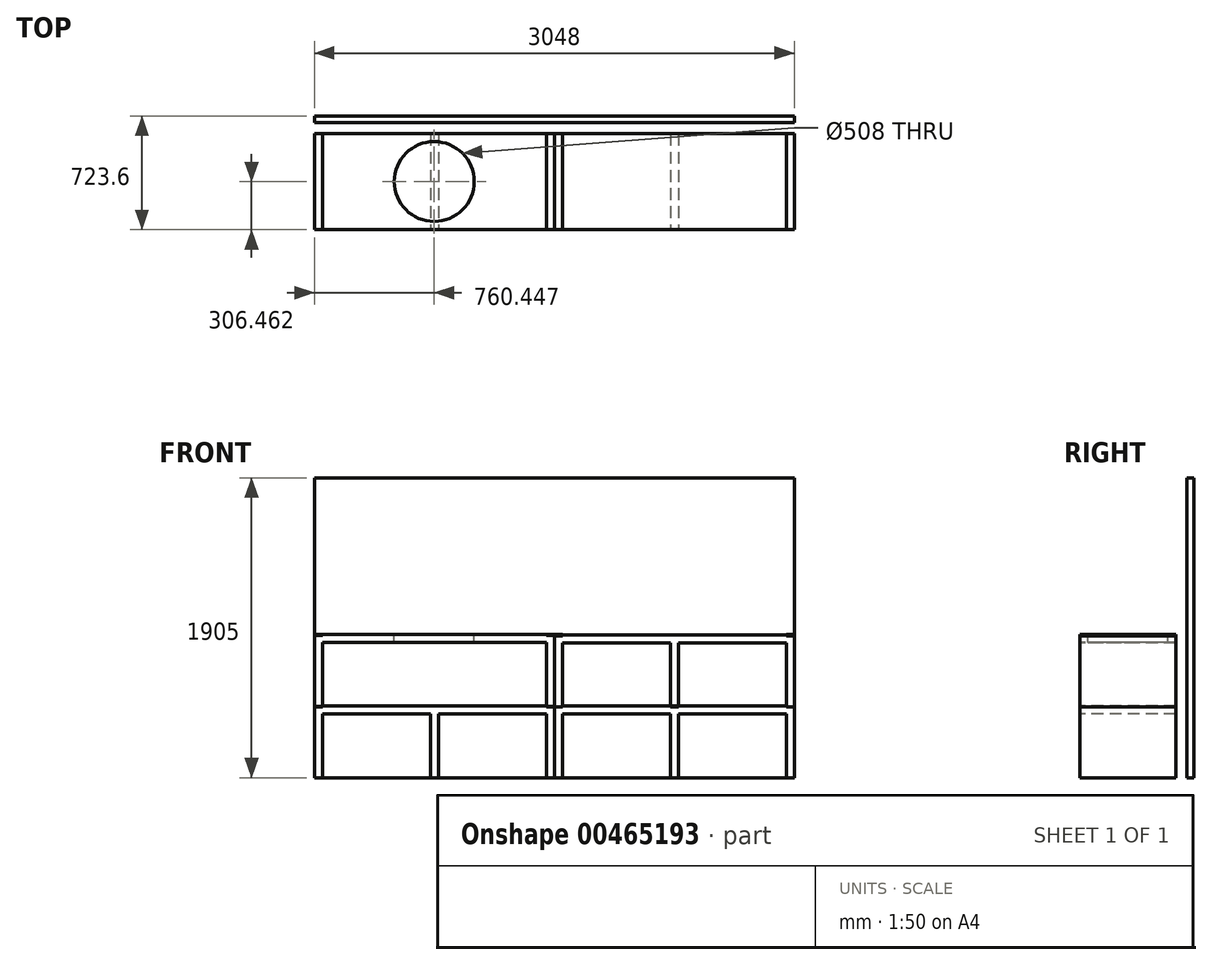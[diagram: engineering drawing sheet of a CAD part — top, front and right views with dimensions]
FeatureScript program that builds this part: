
annotation { "Feature Type Name" : "Feature", "Feature Type Description" : "" }
export const myFeature = defineFeature(function(context is Context, id is Id, definition is map)
    precondition{}
    {
        {
            var Q0;
            Q0=qCreatedBy(makeId("Front.planeOp"),FACE);
            var sketch = newSketch(context, id + "F0", { "sketchPlane" : qUnion([Q0])});
            skLineSegment(sketch, "E0", {"start": v(-50.8, -209.2) * mm, "end": v(-50.8, 241.64) * mm});
            skLineSegment(sketch, "E1", {"start": v(-50.8, 241.64) * mm, "end": v(0, 241.64) * mm});
            skLineSegment(sketch, "E2", {"start": v(0, 241.64) * mm, "end": v(0, 248) * mm});
            skLineSegment(sketch, "E3", {"start": v(0, 248) * mm, "end": v(1422.4, 248) * mm});
            skLineSegment(sketch, "E4", {"start": v(1422.4, 248) * mm, "end": v(1422.4, 241.64) * mm});
            skLineSegment(sketch, "E5", {"start": v(1422.4, 241.64) * mm, "end": v(1473.2, 241.64) * mm});
            skLineSegment(sketch, "E6", {"start": v(1473.2, 241.64) * mm, "end": v(1473.2, -209.2) * mm});
            skLineSegment(sketch, "E7", {"start": v(1473.2, -209.2) * mm, "end": v(1422.4, -209.2) * mm});
            skLineSegment(sketch, "E8", {"start": v(1422.4, -209.2) * mm, "end": v(1422.4, 197.2) * mm});
            skLineSegment(sketch, "E9", {"start": v(1422.4, 197.2) * mm, "end": v(736.6, 197.2) * mm});
            skLineSegment(sketch, "E10", {"start": v(736.6, 197.2) * mm, "end": v(736.6, -209.2) * mm});
            skLineSegment(sketch, "E11", {"start": v(736.6, -209.2) * mm, "end": v(685.8, -209.2) * mm});
            skLineSegment(sketch, "E12", {"start": v(685.8, -209.2) * mm, "end": v(685.8, 197.2) * mm});
            skLineSegment(sketch, "E13", {"start": v(685.8, 197.2) * mm, "end": v(0, 197.2) * mm});
            skLineSegment(sketch, "E14", {"start": v(0, 197.2) * mm, "end": v(0, -209.2) * mm});
            skLineSegment(sketch, "E15", {"start": v(0, -209.2) * mm, "end": v(-50.8, -209.2) * mm});
            skSolve(sketch);
        }
        {
            var Q0;
            Q0 = qSketchRegion(id + "F0", true);
            extrude(context, id + "F1", {"entities" : qUnion([Q0]), "depth" : -609.6 * mm});
        }
        {
            var Q0;
            Q0=makeQuery(id+"F1.opExtrude","CAP_FACE",FACE,{"disambiguationData":[OSD([sQuery(id+"F0.wireOp",EDGE,"E0"),sQuery(id+"F0.wireOp",EDGE,"E1"),sQuery(id+"F0.wireOp",EDGE,"E2"),sQuery(id+"F0.wireOp",EDGE,"E3"),sQuery(id+"F0.wireOp",EDGE,"E4"),sQuery(id+"F0.wireOp",EDGE,"E5"),sQuery(id+"F0.wireOp",EDGE,"E6"),sQuery(id+"F0.wireOp",EDGE,"E7"),sQuery(id+"F0.wireOp",EDGE,"E8"),sQuery(id+"F0.wireOp",EDGE,"E9"),sQuery(id+"F0.wireOp",EDGE,"E10"),sQuery(id+"F0.wireOp",EDGE,"E11"),sQuery(id+"F0.wireOp",EDGE,"E12"),sQuery(id+"F0.wireOp",EDGE,"E13"),sQuery(id+"F0.wireOp",EDGE,"E14"),sQuery(id+"F0.wireOp",EDGE,"E15")])],"isStart":true});
            var sketch = newSketch(context, id + "F2", { "sketchPlane" : qUnion([Q0])});
            skLineSegment(sketch, "E16", {"start": v(-50.8, 273.91) * mm, "end": v(-50.8, 724.76) * mm});
            skLineSegment(sketch, "E17", {"start": v(0, 724.76) * mm, "end": v(-50.8, 724.76) * mm});
            skLineSegment(sketch, "E18", {"start": v(0, 724.76) * mm, "end": v(0, 731.11) * mm});
            skLineSegment(sketch, "E19", {"start": v(0, 731.11) * mm, "end": v(1422.4, 731.11) * mm});
            skLineSegment(sketch, "E20", {"start": v(1422.4, 731.11) * mm, "end": v(1422.4, 724.76) * mm});
            skLineSegment(sketch, "E21", {"start": v(1422.4, 724.76) * mm, "end": v(1473.2, 724.76) * mm});
            skLineSegment(sketch, "E22", {"start": v(1473.2, 724.76) * mm, "end": v(1473.2, 273.91) * mm});
            skLineSegment(sketch, "E23", {"start": v(1473.2, 273.91) * mm, "end": v(1422.4, 273.91) * mm});
            skLineSegment(sketch, "E24", {"start": v(1422.4, 273.91) * mm, "end": v(1422.4, 680.31) * mm});
            skLineSegment(sketch, "E25", {"start": v(1422.4, 680.31) * mm, "end": v(0, 680.31) * mm});
            skLineSegment(sketch, "E26", {"start": v(0, 680.31) * mm, "end": v(0, 273.91) * mm});
            skLineSegment(sketch, "E27", {"start": v(0, 273.91) * mm, "end": v(-50.8, 273.91) * mm});
            skSolve(sketch);
        }
        {
            var Q0;
            Q0 = qSketchRegion(id + "F2", true);
            extrude(context, id + "F3", {"entities" : qUnion([Q0]), "depth" : -609.6 * mm});
        }
        {
            var Q0;
            Q0=makeQuery(id+"F3.opExtrude","SWEPT_BODY",BODY,{"disambiguationData":[OSD([sQuery(id+"F2.wireOp",EDGE,"E16"),sQuery(id+"F2.wireOp",EDGE,"E17"),sQuery(id+"F2.wireOp",EDGE,"E18"),sQuery(id+"F2.wireOp",EDGE,"E19"),sQuery(id+"F2.wireOp",EDGE,"E20"),sQuery(id+"F2.wireOp",EDGE,"E21"),sQuery(id+"F2.wireOp",EDGE,"E22"),sQuery(id+"F2.wireOp",EDGE,"E23"),sQuery(id+"F2.wireOp",EDGE,"E24"),sQuery(id+"F2.wireOp",EDGE,"E25"),sQuery(id+"F2.wireOp",EDGE,"E26"),sQuery(id+"F2.wireOp",EDGE,"E27")])]});
            transform(context, id + "F4", {"entities" : qUnion([Q0]), "transformType" : TransformType.TRANSLATION_3D, "dx" : 0 * mm, "dy" : 0 * mm, "dz" : -31.75 * mm, "makeCopy" : true});
        }
        {
            var Q0;
            Q0=makeQuery(id+"F3.opExtrude","SWEPT_BODY",BODY,{"disambiguationData":[OSD([sQuery(id+"F2.wireOp",EDGE,"E16"),sQuery(id+"F2.wireOp",EDGE,"E17"),sQuery(id+"F2.wireOp",EDGE,"E18"),sQuery(id+"F2.wireOp",EDGE,"E19"),sQuery(id+"F2.wireOp",EDGE,"E20"),sQuery(id+"F2.wireOp",EDGE,"E21"),sQuery(id+"F2.wireOp",EDGE,"E22"),sQuery(id+"F2.wireOp",EDGE,"E23"),sQuery(id+"F2.wireOp",EDGE,"E24"),sQuery(id+"F2.wireOp",EDGE,"E25"),sQuery(id+"F2.wireOp",EDGE,"E26"),sQuery(id+"F2.wireOp",EDGE,"E27")])]});
            deleteBodies(context, id + "F5", {"entities" : qUnion([Q0])});
        }
        {
            var Q0;
            Q0=makeQuery(id+"F4.opPattern","COPY",FACE,{"derivedFrom":makeQuery(id+"F3.opExtrude","SWEPT_FACE",FACE,{"disambiguationData":[OSD([sQuery(id+"F2.wireOp",EDGE,"E19")])]}),"instanceName":"1"});
            var sketch = newSketch(context, id + "F6", { "sketchPlane" : qUnion([Q0])});
            skPoint(sketch, "E28", {"position": v(709.65, 306.46) * mm});
            skSolve(sketch);
        }
        {
            var Q0;
            Q0=sQuery(id+"F6.wireOp",VERTEX,"E28");
            var Q1;
            Q1=makeQuery(id+"F4.opPattern","COPY",BODY,{"derivedFrom":makeQuery(id+"F3.opExtrude","SWEPT_BODY",BODY,{"disambiguationData":[OSD([sQuery(id+"F2.wireOp",EDGE,"E16"),sQuery(id+"F2.wireOp",EDGE,"E17"),sQuery(id+"F2.wireOp",EDGE,"E18"),sQuery(id+"F2.wireOp",EDGE,"E19"),sQuery(id+"F2.wireOp",EDGE,"E20"),sQuery(id+"F2.wireOp",EDGE,"E21"),sQuery(id+"F2.wireOp",EDGE,"E22"),sQuery(id+"F2.wireOp",EDGE,"E23"),sQuery(id+"F2.wireOp",EDGE,"E24"),sQuery(id+"F2.wireOp",EDGE,"E25"),sQuery(id+"F2.wireOp",EDGE,"E26"),sQuery(id+"F2.wireOp",EDGE,"E27")])]}),"instanceName":"1"});
            hole(context, id + "F7", {"style" : HoleStyle.SIMPLE, "endStyle" : HoleEndStyle.BLIND, "holeDiameter" : 508 * mm, "holeDepth" : 50.8 * mm, "isTappedThrough" : true, "tappedDepth" : 12.7 * mm, "tapClearance" : 3, "locations" : qUnion([Q0]), "scope" : qUnion([Q1])});
        }
        {
            var Q0;
            Q0=makeQuery(id+"F4.opPattern","COPY",FACE,{"derivedFrom":makeQuery(id+"F3.opExtrude","CAP_FACE",FACE,{"disambiguationData":[OSD([sQuery(id+"F2.wireOp",EDGE,"E16"),sQuery(id+"F2.wireOp",EDGE,"E17"),sQuery(id+"F2.wireOp",EDGE,"E18"),sQuery(id+"F2.wireOp",EDGE,"E19"),sQuery(id+"F2.wireOp",EDGE,"E20"),sQuery(id+"F2.wireOp",EDGE,"E21"),sQuery(id+"F2.wireOp",EDGE,"E22"),sQuery(id+"F2.wireOp",EDGE,"E23"),sQuery(id+"F2.wireOp",EDGE,"E24"),sQuery(id+"F2.wireOp",EDGE,"E25"),sQuery(id+"F2.wireOp",EDGE,"E26"),sQuery(id+"F2.wireOp",EDGE,"E27")])],"isStart":true}),"instanceName":"1"});
            var sketch = newSketch(context, id + "F8", { "sketchPlane" : qUnion([Q0])});
            skLineSegment(sketch, "E29.bottom", {"start": v(-50.8, 727.26) * mm, "end": v(0, 727.26) * mm});
            skLineSegment(sketch, "E29.top", {"start": v(-50.8, 720.91) * mm, "end": v(0, 720.91) * mm});
            skLineSegment(sketch, "E29.left", {"start": v(-50.8, 727.26) * mm, "end": v(-50.8, 720.91) * mm});
            skLineSegment(sketch, "E29.right", {"start": v(0, 727.26) * mm, "end": v(0, 720.91) * mm});
            skSolve(sketch);
        }
        {
            var Q0;
            Q0 = qSketchRegion(id + "F8", true);
            extrude(context, id + "F9", {"entities" : qUnion([Q0]), "depth" : -609.6 * mm});
        }
        {
            var Q0;
            Q0=makeQuery(id+"F9.opExtrude","SWEPT_BODY",BODY,{"disambiguationData":[OSD([sQuery(id+"F8.wireOp",EDGE,"E29.bottom"),sQuery(id+"F8.wireOp",EDGE,"E29.top"),sQuery(id+"F8.wireOp",EDGE,"E29.left"),sQuery(id+"F8.wireOp",EDGE,"E29.right")])]});
            transform(context, id + "F10", {"entities" : qUnion([Q0]), "transformType" : TransformType.TRANSLATION_3D, "dx" : 0 * mm, "dy" : 0 * mm, "dz" : -27.94 * mm, "makeCopy" : true});
        }
        {
            var Q0;
            Q0=makeQuery(id+"F9.opExtrude","SWEPT_BODY",BODY,{"disambiguationData":[OSD([sQuery(id+"F8.wireOp",EDGE,"E29.bottom"),sQuery(id+"F8.wireOp",EDGE,"E29.top"),sQuery(id+"F8.wireOp",EDGE,"E29.left"),sQuery(id+"F8.wireOp",EDGE,"E29.right")])]});
            deleteBodies(context, id + "F11", {"entities" : qUnion([Q0])});
        }
        {
            var Q0;
            Q0=makeQuery(id+"F10.opPattern","COPY",BODY,{"derivedFrom":makeQuery(id+"F9.opExtrude","SWEPT_BODY",BODY,{"disambiguationData":[OSD([sQuery(id+"F8.wireOp",EDGE,"E29.bottom"),sQuery(id+"F8.wireOp",EDGE,"E29.top"),sQuery(id+"F8.wireOp",EDGE,"E29.left"),sQuery(id+"F8.wireOp",EDGE,"E29.right")])]}),"instanceName":"1"});
            transform(context, id + "F12", {"entities" : qUnion([Q0]), "transformType" : TransformType.TRANSLATION_3D, "dx" : 1473.2 * mm, "dy" : 254 * mm, "dz" : 0 * mm, "makeCopy" : true});
        }
        {
            var Q0;
            Q0=makeQuery(id+"F1.opExtrude","SWEPT_BODY",BODY,{"disambiguationData":[OSD([sQuery(id+"F0.wireOp",EDGE,"E0"),sQuery(id+"F0.wireOp",EDGE,"E1"),sQuery(id+"F0.wireOp",EDGE,"E2"),sQuery(id+"F0.wireOp",EDGE,"E3"),sQuery(id+"F0.wireOp",EDGE,"E4"),sQuery(id+"F0.wireOp",EDGE,"E5"),sQuery(id+"F0.wireOp",EDGE,"E6"),sQuery(id+"F0.wireOp",EDGE,"E7"),sQuery(id+"F0.wireOp",EDGE,"E8"),sQuery(id+"F0.wireOp",EDGE,"E9"),sQuery(id+"F0.wireOp",EDGE,"E10"),sQuery(id+"F0.wireOp",EDGE,"E11"),sQuery(id+"F0.wireOp",EDGE,"E12"),sQuery(id+"F0.wireOp",EDGE,"E13"),sQuery(id+"F0.wireOp",EDGE,"E14"),sQuery(id+"F0.wireOp",EDGE,"E15")])]});
            transform(context, id + "F13", {"entities" : qUnion([Q0]), "transformType" : TransformType.TRANSLATION_3D, "dx" : 1524 * mm, "dy" : 0 * mm, "dz" : 0 * mm, "makeCopy" : true});
        }
        {
            var Q0;
            Q0=makeQuery(id+"F13.opPattern","COPY",BODY,{"derivedFrom":makeQuery(id+"F1.opExtrude","SWEPT_BODY",BODY,{"disambiguationData":[OSD([sQuery(id+"F0.wireOp",EDGE,"E0"),sQuery(id+"F0.wireOp",EDGE,"E1"),sQuery(id+"F0.wireOp",EDGE,"E2"),sQuery(id+"F0.wireOp",EDGE,"E3"),sQuery(id+"F0.wireOp",EDGE,"E4"),sQuery(id+"F0.wireOp",EDGE,"E5"),sQuery(id+"F0.wireOp",EDGE,"E6"),sQuery(id+"F0.wireOp",EDGE,"E7"),sQuery(id+"F0.wireOp",EDGE,"E8"),sQuery(id+"F0.wireOp",EDGE,"E9"),sQuery(id+"F0.wireOp",EDGE,"E10"),sQuery(id+"F0.wireOp",EDGE,"E11"),sQuery(id+"F0.wireOp",EDGE,"E12"),sQuery(id+"F0.wireOp",EDGE,"E13"),sQuery(id+"F0.wireOp",EDGE,"E14"),sQuery(id+"F0.wireOp",EDGE,"E15")])]}),"instanceName":"1"});
            transform(context, id + "F14", {"entities" : qUnion([Q0]), "transformType" : TransformType.TRANSLATION_3D, "dx" : 0 * mm, "dy" : 0 * mm, "dz" : 450.85 * mm, "makeCopy" : true});
        }
        {
            var Q0;
            Q0=makeQuery(id+"F12.opPattern","COPY",BODY,{"derivedFrom":makeQuery(id+"F10.opPattern","COPY",BODY,{"derivedFrom":makeQuery(id+"F9.opExtrude","SWEPT_BODY",BODY,{"disambiguationData":[OSD([sQuery(id+"F8.wireOp",EDGE,"E29.bottom"),sQuery(id+"F8.wireOp",EDGE,"E29.top"),sQuery(id+"F8.wireOp",EDGE,"E29.left"),sQuery(id+"F8.wireOp",EDGE,"E29.right")])]}),"instanceName":"1"}),"instanceName":"1"});
            transform(context, id + "F15", {"entities" : qUnion([Q0]), "transformType" : TransformType.TRANSLATION_3D, "dx" : 50.8 * mm, "dy" : 0 * mm, "dz" : 0 * mm, "makeCopy" : true});
        }
        {
            var Q0;
            Q0=makeQuery(id+"F12.opPattern","COPY",BODY,{"derivedFrom":makeQuery(id+"F10.opPattern","COPY",BODY,{"derivedFrom":makeQuery(id+"F9.opExtrude","SWEPT_BODY",BODY,{"disambiguationData":[OSD([sQuery(id+"F8.wireOp",EDGE,"E29.bottom"),sQuery(id+"F8.wireOp",EDGE,"E29.top"),sQuery(id+"F8.wireOp",EDGE,"E29.left"),sQuery(id+"F8.wireOp",EDGE,"E29.right")])]}),"instanceName":"1"}),"instanceName":"1"});
            transform(context, id + "F16", {"entities" : qUnion([Q0]), "transformType" : TransformType.TRANSLATION_3D, "dx" : 1524 * mm, "dy" : 0 * mm, "dz" : 0 * mm, "makeCopy" : true});
        }
        {
            var Q0;
            Q0=makeQuery(id+"F12.opPattern","COPY",BODY,{"derivedFrom":makeQuery(id+"F10.opPattern","COPY",BODY,{"derivedFrom":makeQuery(id+"F9.opExtrude","SWEPT_BODY",BODY,{"disambiguationData":[OSD([sQuery(id+"F8.wireOp",EDGE,"E29.bottom"),sQuery(id+"F8.wireOp",EDGE,"E29.top"),sQuery(id+"F8.wireOp",EDGE,"E29.left"),sQuery(id+"F8.wireOp",EDGE,"E29.right")])]}),"instanceName":"1"}),"instanceName":"1"});
            var Q1;
            Q1=makeQuery(id+"F15.opPattern","COPY",BODY,{"derivedFrom":makeQuery(id+"F12.opPattern","COPY",BODY,{"derivedFrom":makeQuery(id+"F10.opPattern","COPY",BODY,{"derivedFrom":makeQuery(id+"F9.opExtrude","SWEPT_BODY",BODY,{"disambiguationData":[OSD([sQuery(id+"F8.wireOp",EDGE,"E29.bottom"),sQuery(id+"F8.wireOp",EDGE,"E29.top"),sQuery(id+"F8.wireOp",EDGE,"E29.left"),sQuery(id+"F8.wireOp",EDGE,"E29.right")])]}),"instanceName":"1"}),"instanceName":"1"}),"instanceName":"1"});
            var Q2;
            Q2=makeQuery(id+"F16.opPattern","COPY",BODY,{"derivedFrom":makeQuery(id+"F12.opPattern","COPY",BODY,{"derivedFrom":makeQuery(id+"F10.opPattern","COPY",BODY,{"derivedFrom":makeQuery(id+"F9.opExtrude","SWEPT_BODY",BODY,{"disambiguationData":[OSD([sQuery(id+"F8.wireOp",EDGE,"E29.bottom"),sQuery(id+"F8.wireOp",EDGE,"E29.top"),sQuery(id+"F8.wireOp",EDGE,"E29.left"),sQuery(id+"F8.wireOp",EDGE,"E29.right")])]}),"instanceName":"1"}),"instanceName":"1"}),"instanceName":"1"});
            deleteBodies(context, id + "F17", {"entities" : qUnion([Q0, Q1, Q2])});
        }
        {
            var Q0;
            Q0=makeQuery(id+"F10.opPattern","COPY",BODY,{"derivedFrom":makeQuery(id+"F9.opExtrude","SWEPT_BODY",BODY,{"disambiguationData":[OSD([sQuery(id+"F8.wireOp",EDGE,"E29.bottom"),sQuery(id+"F8.wireOp",EDGE,"E29.top"),sQuery(id+"F8.wireOp",EDGE,"E29.left"),sQuery(id+"F8.wireOp",EDGE,"E29.right")])]}),"instanceName":"1"});
            transform(context, id + "F18", {"entities" : qUnion([Q0]), "transformType" : TransformType.TRANSLATION_3D, "dx" : 1473.2 * mm, "dy" : 0 * mm, "dz" : 0 * mm, "makeCopy" : true});
        }
        {
            var Q0;
            Q0=makeQuery(id+"F18.opPattern","COPY",BODY,{"derivedFrom":makeQuery(id+"F10.opPattern","COPY",BODY,{"derivedFrom":makeQuery(id+"F9.opExtrude","SWEPT_BODY",BODY,{"disambiguationData":[OSD([sQuery(id+"F8.wireOp",EDGE,"E29.bottom"),sQuery(id+"F8.wireOp",EDGE,"E29.top"),sQuery(id+"F8.wireOp",EDGE,"E29.left"),sQuery(id+"F8.wireOp",EDGE,"E29.right")])]}),"instanceName":"1"}),"instanceName":"1"});
            transform(context, id + "F19", {"entities" : qUnion([Q0]), "transformType" : TransformType.TRANSLATION_3D, "dx" : 50.8 * mm, "dy" : 0 * mm, "dz" : 0 * mm, "makeCopy" : true});
        }
        {
            var Q0;
            Q0=makeQuery(id+"F18.opPattern","COPY",BODY,{"derivedFrom":makeQuery(id+"F10.opPattern","COPY",BODY,{"derivedFrom":makeQuery(id+"F9.opExtrude","SWEPT_BODY",BODY,{"disambiguationData":[OSD([sQuery(id+"F8.wireOp",EDGE,"E29.bottom"),sQuery(id+"F8.wireOp",EDGE,"E29.top"),sQuery(id+"F8.wireOp",EDGE,"E29.left"),sQuery(id+"F8.wireOp",EDGE,"E29.right")])]}),"instanceName":"1"}),"instanceName":"1"});
            transform(context, id + "F20", {"entities" : qUnion([Q0]), "transformType" : TransformType.TRANSLATION_3D, "dx" : 1524 * mm, "dy" : 0 * mm, "dz" : 0 * mm, "makeCopy" : true});
        }
        {
            var Q0;
            Q0=makeQuery(id+"F13.opPattern","COPY",FACE,{"derivedFrom":makeQuery(id+"F1.opExtrude","SWEPT_FACE",FACE,{"disambiguationData":[OSD([sQuery(id+"F0.wireOp",EDGE,"E6")])]}),"instanceName":"1"});
            var sketch = newSketch(context, id + "F21", { "sketchPlane" : qUnion([Q0])});
            skLineSegment(sketch, "E30.bottom", {"start": v(680.42, -209.2) * mm, "end": v(723.6, -209.2) * mm});
            skLineSegment(sketch, "E30.top", {"start": v(680.42, 1695.8) * mm, "end": v(723.6, 1695.8) * mm});
            skLineSegment(sketch, "E30.left", {"start": v(680.42, -209.2) * mm, "end": v(680.42, 1695.8) * mm});
            skLineSegment(sketch, "E30.right", {"start": v(723.6, -209.2) * mm, "end": v(723.6, 1695.8) * mm});
            skSolve(sketch);
        }
        {
            var Q0;
            Q0 = qSketchRegion(id + "F21", true);
            extrude(context, id + "F22", {"entities" : qUnion([Q0]), "depth" : -3048 * mm});
        }
    });
